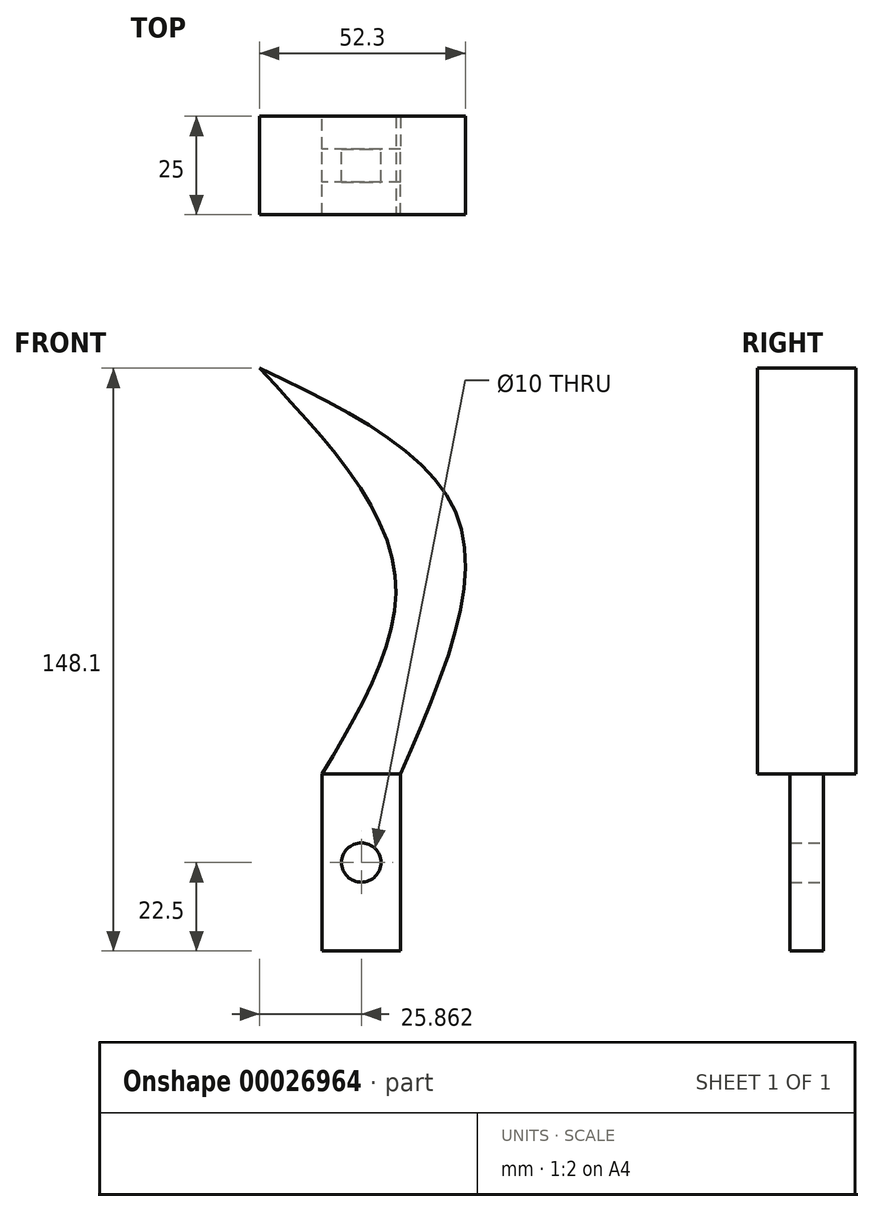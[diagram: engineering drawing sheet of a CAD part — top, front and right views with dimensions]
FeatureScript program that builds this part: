
annotation { "Feature Type Name" : "Feature", "Feature Type Description" : "" }
export const myFeature = defineFeature(function(context is Context, id is Id, definition is map)
    precondition{}
    {
        {
            var Q0;
            Q0=qCreatedBy(makeId("Front.planeOp"),FACE);
            var sketch = newSketch(context, id + "F0", { "sketchPlane" : qUnion([Q0])});
            skFitSpline(sketch, "E0", {"points": [v(0, 103.1) * mm, v(50.34, 65.17) * mm, v(35.86, 0) * mm], "startDerivative": vector(134.37, -64.27) * mm, "endDerivative": vector(-61.7, -141.57) * mm});
            skLineSegment(sketch, "E1", {"start": v(35.86, 0) * mm, "end": v(35.86, -45) * mm});
            skLineSegment(sketch, "E2", {"start": v(35.86, -45) * mm, "end": v(15.86, -45) * mm});
            skLineSegment(sketch, "E3", {"start": v(15.86, -45) * mm, "end": v(15.86, 0) * mm});
            skCircle(sketch, "E4", {"center": v(25.86, -22.5) * mm, "radius": 5 * mm});
            skFitSpline(sketch, "E5", {"points": [v(15.86, 0) * mm, v(34.4, 50.8) * mm, v(0, 103.1) * mm], "startDerivative": vector(63.71, 106.55) * mm, "endDerivative": vector(-93.52, 99.74) * mm});
            skSolve(sketch);
        }
        {
            var Q0;
            Q0=makeQuery(id+"F0.imprint","IMPRINT",FACE,{"disambiguationData":[TD([[makeQuery(id+"F0.imprint","IMPRINT",EDGE,{"derivedFrom":sQuery(id+"F0.wireOp",EDGE,"E0")}),-1.0]])]});
            extrude(context, id + "F1", {"entities" : qUnion([Q0]), "depth" : 25 * mm});
        }
        {
            var Q0;
            Q0=makeQuery(id+"F1.opExtrude","SWEPT_FACE",FACE,{"disambiguationData":[OSD([sQuery(id+"F0.wireOp",EDGE,"E3")])]});
            var sketch = newSketch(context, id + "F2", { "sketchPlane" : qUnion([Q0])});
            skLineSegment(sketch, "E6", {"start": v(0, 0) * mm, "end": v(25, 0) * mm});
            skLineSegment(sketch, "E7", {"start": v(8.3, 0) * mm, "end": v(8.3, -45) * mm});
            skLineSegment(sketch, "E8", {"start": v(16.7, 0) * mm, "end": v(16.7, -45) * mm});
            skSolve(sketch);
        }
        {
            var Q0;
            {var subQ2=sQuery(id+"F2.wireOp",EDGE,"E7");Q0=makeQuery(id+"F2.imprint","IMPRINT",FACE,{"disambiguationData":[TD([[makeQuery(id+"F2.imprint","IMPRINT",EDGE,{"derivedFrom":subQ2}),-1.0]])]});}
            var Q1;
            {var subQ2=sQuery(id+"F2.wireOp",EDGE,"E8");Q1=makeQuery(id+"F2.imprint","IMPRINT",FACE,{"disambiguationData":[TD([[makeQuery(id+"F2.imprint","IMPRINT",EDGE,{"derivedFrom":subQ2}),1.0]])]});}
            extrude(context, id + "F3", {"entities" : qUnion([Q0, Q1]), "operationType" : NewBodyOperationType.REMOVE, "endBound" : BoundingType.THROUGH_ALL, "oppositeDirection" : true, "depth" : 25 * mm});
        }
    });
